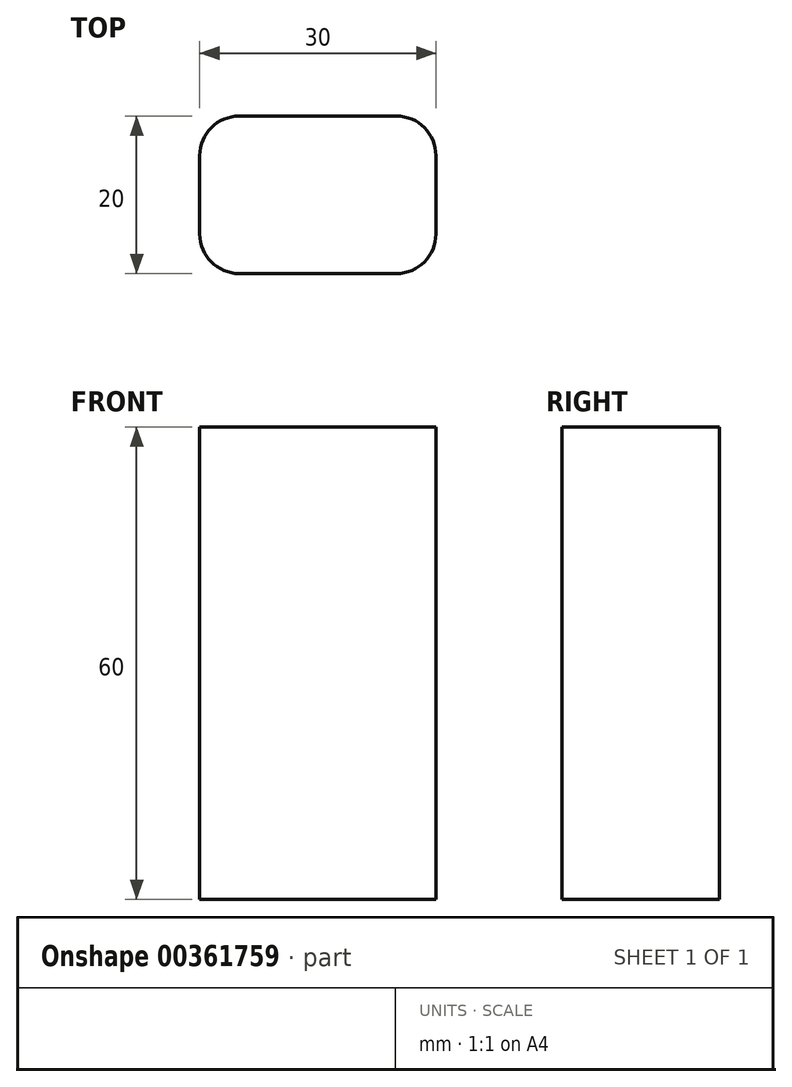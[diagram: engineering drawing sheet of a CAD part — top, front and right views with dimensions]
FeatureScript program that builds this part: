
annotation { "Feature Type Name" : "Feature", "Feature Type Description" : "" }
export const myFeature = defineFeature(function(context is Context, id is Id, definition is map)
    precondition{}
    {
        {
            var Q0;
            Q0=qCreatedBy(makeId("Top.planeOp"),FACE);
            var sketch = newSketch(context, id + "F0", { "sketchPlane" : qUnion([Q0])});
            skLineSegment(sketch, "E0.bottom", {"start": v(-13.91, -7.42) * mm, "end": v(16.09, -7.42) * mm});
            skLineSegment(sketch, "E0.top", {"start": v(-13.91, 12.58) * mm, "end": v(16.09, 12.58) * mm});
            skLineSegment(sketch, "E0.left", {"start": v(-13.91, -7.42) * mm, "end": v(-13.91, 12.58) * mm});
            skLineSegment(sketch, "E0.right", {"start": v(16.09, -7.42) * mm, "end": v(16.09, 12.58) * mm});
            skSolve(sketch);
        }
        {
            var Q0;
            Q0 = qSketchRegion(id + "F0", true);
            var Q1;
            Q1=makeQuery(id+"F0.imprint","IMPRINT",FACE,{"disambiguationData":[TD([[makeQuery(id+"F0.imprint","IMPRINT",EDGE,{"derivedFrom":sQuery(id+"F0.wireOp",EDGE,"E0.bottom")}),1.0]])]});
            extrude(context, id + "F1", {"entities" : qUnion([Q0, Q1]), "depth" : 60 * mm});
        }
        {
            var Q0;
            Q0=makeQuery(id+"F1.opExtrude","SWEPT_EDGE",EDGE,{"disambiguationData":[OSD([sQuery(id+"F0.wireOp",EDGE,"E0.bottom"),sQuery(id+"F0.wireOp",EDGE,"E0.left")])]});
            var Q1;
            Q1=makeQuery(id+"F1.opExtrude","SWEPT_EDGE",EDGE,{"disambiguationData":[OSD([sQuery(id+"F0.wireOp",EDGE,"E0.top"),sQuery(id+"F0.wireOp",EDGE,"E0.left")])]});
            var Q2;
            Q2=makeQuery(id+"F1.opExtrude","SWEPT_EDGE",EDGE,{"disambiguationData":[OSD([sQuery(id+"F0.wireOp",EDGE,"E0.bottom"),sQuery(id+"F0.wireOp",EDGE,"E0.right")])]});
            var Q3;
            Q3=makeQuery(id+"F1.opExtrude","SWEPT_EDGE",EDGE,{"disambiguationData":[OSD([sQuery(id+"F0.wireOp",EDGE,"E0.top"),sQuery(id+"F0.wireOp",EDGE,"E0.right")])]});
            fillet(context, id + "F2", {"entities" : qUnion([Q0, Q1, Q2, Q3]), "radius" : 5 * mm, "tangentPropagation" : true, "allowEdgeOverflow" : false});
        }
    });
